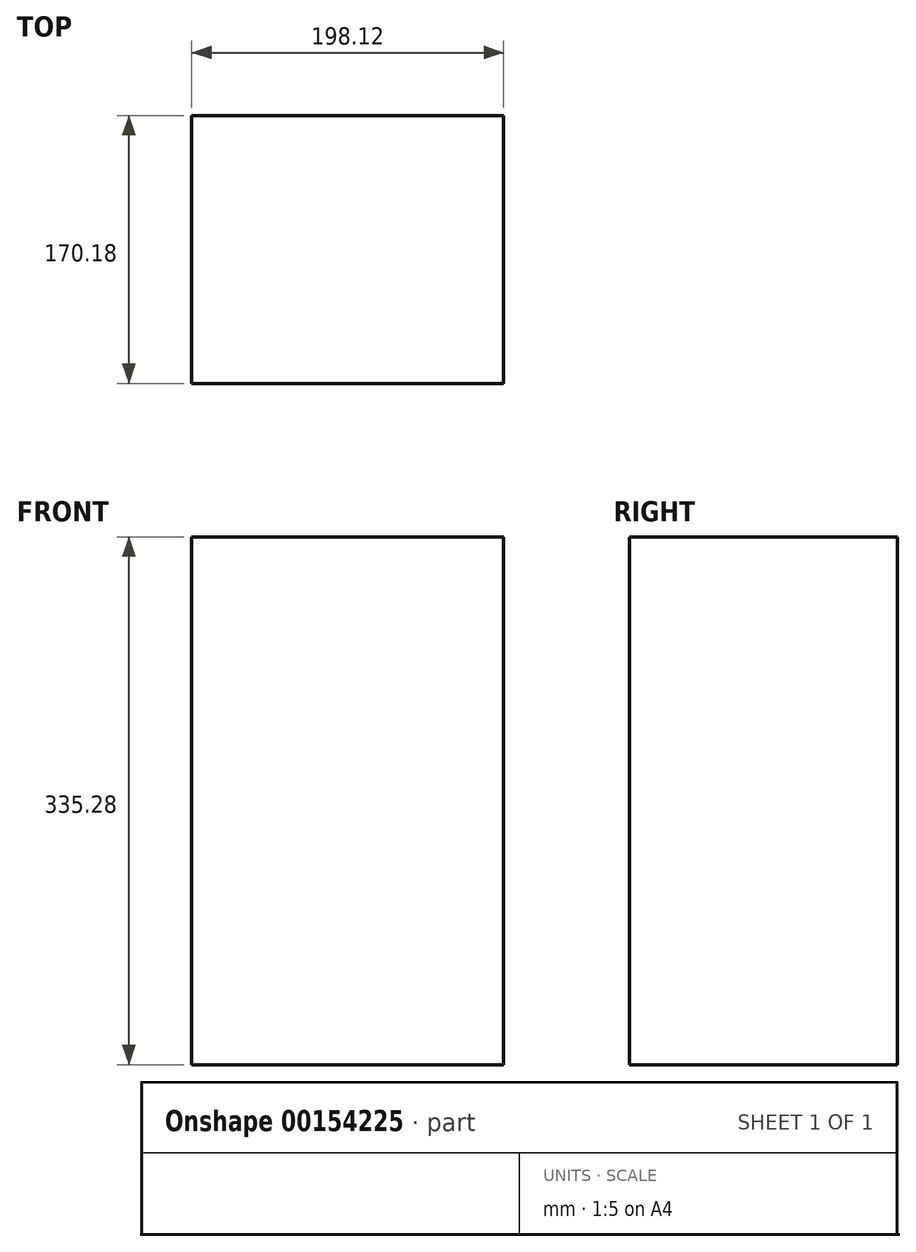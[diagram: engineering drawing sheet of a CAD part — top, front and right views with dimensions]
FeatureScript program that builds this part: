
annotation { "Feature Type Name" : "Feature", "Feature Type Description" : "" }
export const myFeature = defineFeature(function(context is Context, id is Id, definition is map)
    precondition{}
    {
        {
            var Q0;
            Q0=qCreatedBy(makeId("Top.planeOp"),FACE);
            var sketch = newSketch(context, id + "F0", { "sketchPlane" : qUnion([Q0])});
            skLineSegment(sketch, "E0.bottom", {"start": v(99.06, 87.05) * mm, "end": v(-99.06, 87.05) * mm});
            skLineSegment(sketch, "E0.top", {"start": v(99.06, -83.13) * mm, "end": v(-99.06, -83.13) * mm});
            skLineSegment(sketch, "E0.left", {"start": v(99.06, 87.05) * mm, "end": v(99.06, -83.13) * mm});
            skLineSegment(sketch, "E0.right", {"start": v(-99.06, 87.05) * mm, "end": v(-99.06, -83.13) * mm});
            skPoint(sketch, "E0.middle", {"position": v(0, 1.96) * mm});
            skSolve(sketch);
        }
        {
            var Q0;
            Q0=makeQuery(id+"F0.imprint","IMPRINT",FACE,{"disambiguationData":[TD([[makeQuery(id+"F0.imprint","IMPRINT",EDGE,{"derivedFrom":sQuery(id+"F0.wireOp",EDGE,"E0.bottom")}),1.0]])]});
            extrude(context, id + "F1", {"entities" : qUnion([Q0]), "depth" : 335.28 * mm});
        }
    });
